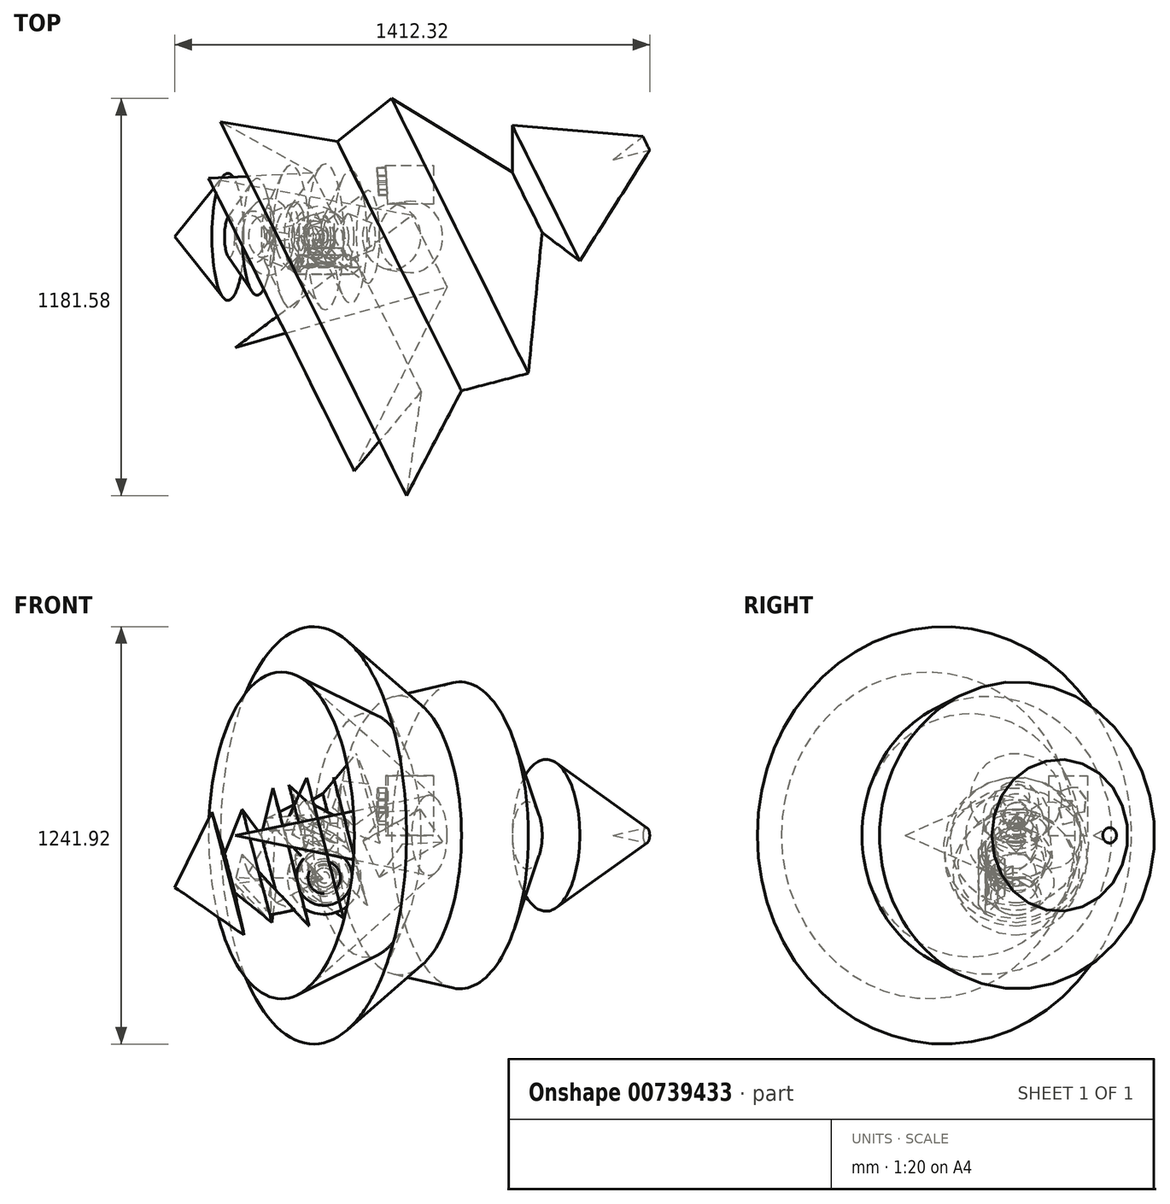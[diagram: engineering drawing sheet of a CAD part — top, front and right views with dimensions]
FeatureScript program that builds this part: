
annotation { "Feature Type Name" : "Feature", "Feature Type Description" : "" }
export const myFeature = defineFeature(function(context is Context, id is Id, definition is map)
    precondition{}
    {
        {
            var Q0;
            Q0=qCreatedBy(makeId("Front.planeOp"),FACE);
            var sketch = newSketch(context, id + "F0", { "sketchPlane" : qUnion([Q0])});
            skLineSegment(sketch, "E0", {"start": v(-2.63, 51.59) * mm, "end": v(-55.72, -50.08) * mm});
            skLineSegment(sketch, "E1", {"start": v(-55.72, -50.08) * mm, "end": v(-14.15, -31.55) * mm});
            skLineSegment(sketch, "E2", {"start": v(-14.15, -31.55) * mm, "end": v(-23.57, -10.42) * mm});
            skLineSegment(sketch, "E3", {"start": v(-23.57, -10.42) * mm, "end": v(10.4, -53.09) * mm});
            skLineSegment(sketch, "E4", {"start": v(10.4, -53.09) * mm, "end": v(32.93, -22.29) * mm});
            skLineSegment(sketch, "E5", {"start": v(32.93, -22.29) * mm, "end": v(13.65, -17.28) * mm});
            skLineSegment(sketch, "E6", {"start": v(13.65, -17.28) * mm, "end": v(30.68, 3.5) * mm});
            skLineSegment(sketch, "E7", {"start": v(30.68, 3.5) * mm, "end": v(61.07, -21.4) * mm});
            skLineSegment(sketch, "E8", {"start": v(61.07, -21.4) * mm, "end": v(73.25, 36.31) * mm});
            skLineSegment(sketch, "E9", {"start": v(73.25, 36.31) * mm, "end": v(11.4, 36.31) * mm});
            skLineSegment(sketch, "E10", {"start": v(11.4, 36.31) * mm, "end": v(0.63, -7.51) * mm});
            skLineSegment(sketch, "E11", {"start": v(0.63, -7.51) * mm, "end": v(-2.63, 51.59) * mm});
            skSolve(sketch);
        }
        {
            var Q0;
            Q0=makeQuery(id+"F0.imprint","IMPRINT",FACE,{"disambiguationData":[TD([[makeQuery(id+"F0.imprint","IMPRINT",EDGE,{"derivedFrom":sQuery(id+"F0.wireOp",EDGE,"E0")}),1.0]])]});
            var Q1;
            Q1=sQuery(id+"F0.wireOp",EDGE,"E0");
            revolve(context, id + "F1", {"surfaceOperationType" : NewSurfaceOperationType.NEW, "entities" : qUnion([Q0]), "axis" : qUnion([Q1]), "revolveType" : RevolveType.FULL});
        }
        {
            var Q0;
            Q0=qCreatedBy(makeId("Right.planeOp"),FACE);
            var sketch = newSketch(context, id + "F2", { "sketchPlane" : qUnion([Q0])});
            skLineSegment(sketch, "E12", {"start": v(-33.87, -70.47) * mm, "end": v(-87.06, -44.3) * mm});
            skLineSegment(sketch, "E13", {"start": v(-87.06, -44.3) * mm, "end": v(-53.53, -50.85) * mm});
            skLineSegment(sketch, "E14", {"start": v(-53.53, -50.85) * mm, "end": v(-90.7, -16.17) * mm});
            skLineSegment(sketch, "E15", {"start": v(-90.7, -16.17) * mm, "end": v(-110.94, -42.5) * mm});
            skLineSegment(sketch, "E16", {"start": v(-110.94, -42.5) * mm, "end": v(-80.24, -77.64) * mm});
            skLineSegment(sketch, "E17", {"start": v(-80.24, -77.64) * mm, "end": v(-88.69, -125.64) * mm});
            skLineSegment(sketch, "E18", {"start": v(-88.69, -125.64) * mm, "end": v(-55.2, -125.64) * mm});
            skLineSegment(sketch, "E19", {"start": v(-55.2, -125.64) * mm, "end": v(-75.07, -97.2) * mm});
            skLineSegment(sketch, "E20", {"start": v(-75.07, -97.2) * mm, "end": v(-62.68, -85.31) * mm});
            skLineSegment(sketch, "E21", {"start": v(-62.68, -85.31) * mm, "end": v(-31.96, -109.17) * mm});
            skLineSegment(sketch, "E22", {"start": v(-31.96, -109.17) * mm, "end": v(-9.41, -89.97) * mm});
            skLineSegment(sketch, "E23", {"start": v(-9.41, -89.97) * mm, "end": v(-33.87, -97.57) * mm});
            skLineSegment(sketch, "E24", {"start": v(-33.87, -97.57) * mm, "end": v(-33.87, -70.47) * mm});
            skSolve(sketch);
        }
        {
            var Q0;
            Q0=makeQuery(id+"F2.imprint","IMPRINT",FACE,{"disambiguationData":[TD([[makeQuery(id+"F2.imprint","IMPRINT",EDGE,{"derivedFrom":sQuery(id+"F2.wireOp",EDGE,"E12")}),1.0]])]});
            var Q1;
            Q1=sQuery(id+"F2.wireOp",EDGE,"E18");
            revolve(context, id + "F3", {"surfaceOperationType" : NewSurfaceOperationType.NEW, "entities" : qUnion([Q0]), "axis" : qUnion([Q1]), "revolveType" : RevolveType.FULL});
        }
        {
            var Q0;
            Q0=qCreatedBy(makeId("Front.planeOp"),FACE);
            var sketch = newSketch(context, id + "F4", { "sketchPlane" : qUnion([Q0])});
            skLineSegment(sketch, "E25", {"start": v(178.62, 69.18) * mm, "end": v(114.89, -17.47) * mm});
            skLineSegment(sketch, "E26", {"start": v(114.89, -17.47) * mm, "end": v(162.96, -124.25) * mm});
            skLineSegment(sketch, "E27", {"start": v(162.96, -124.25) * mm, "end": v(231.73, -26.42) * mm});
            skLineSegment(sketch, "E28", {"start": v(231.73, -26.42) * mm, "end": v(178.62, 69.18) * mm});
            skSolve(sketch);
        }
        {
            var Q0;
            Q0=makeQuery(id+"F4.imprint","IMPRINT",FACE,{"disambiguationData":[TD([[makeQuery(id+"F4.imprint","IMPRINT",EDGE,{"derivedFrom":sQuery(id+"F4.wireOp",EDGE,"E25")}),1.0]])]});
            var Q1;
            Q1=sQuery(id+"F4.wireOp",EDGE,"E28");
            revolve(context, id + "F5", {"surfaceOperationType" : NewSurfaceOperationType.NEW, "entities" : qUnion([Q0]), "axis" : qUnion([Q1]), "revolveType" : RevolveType.FULL});
        }
        {
            var Q0;
            Q0=qCreatedBy(makeId("Front.planeOp"),FACE);
            var sketch = newSketch(context, id + "F6", { "sketchPlane" : qUnion([Q0])});
            skLineSegment(sketch, "E29", {"start": v(-225.5, -112.51) * mm, "end": v(-146.12, 21.1) * mm});
            skLineSegment(sketch, "E30", {"start": v(-146.12, 21.1) * mm, "end": v(-151.15, -125.37) * mm});
            skLineSegment(sketch, "E31", {"start": v(-151.15, -125.37) * mm, "end": v(-228.86, -198.6) * mm});
            skLineSegment(sketch, "E32", {"start": v(-228.86, -198.6) * mm, "end": v(-264.64, -144.38) * mm});
            skLineSegment(sketch, "E33", {"start": v(-264.64, -144.38) * mm, "end": v(-176.87, -132.64) * mm});
            skLineSegment(sketch, "E34", {"start": v(-176.87, -132.64) * mm, "end": v(-262.4, -125.93) * mm});
            skLineSegment(sketch, "E35", {"start": v(-262.4, -125.93) * mm, "end": v(-243.96, -56.6) * mm});
            skLineSegment(sketch, "E36", {"start": v(-243.96, -56.6) * mm, "end": v(-225.5, -112.51) * mm});
            skSolve(sketch);
        }
        {
            var Q0;
            Q0 = qSketchRegion(id + "F6", true);
            var Q1;
            Q1=sQuery(id+"F6.wireOp",EDGE,"E31");
            revolve(context, id + "F7", {"operationType" : NewBodyOperationType.ADD, "surfaceOperationType" : NewSurfaceOperationType.NEW, "entities" : qUnion([Q0]), "axis" : qUnion([Q1]), "revolveType" : RevolveType.FULL});
        }
        {
            var Q0;
            Q0=qCreatedBy(makeId("Front.planeOp"),FACE);
            var sketch = newSketch(context, id + "F8", { "sketchPlane" : qUnion([Q0])});
            skLineSegment(sketch, "E37", {"start": v(19.88, 31.76) * mm, "end": v(165.14, -22.85) * mm});
            skLineSegment(sketch, "E38", {"start": v(165.14, -22.85) * mm, "end": v(152.75, 74) * mm});
            skLineSegment(sketch, "E39", {"start": v(152.75, 74) * mm, "end": v(88.57, 28.39) * mm});
            skLineSegment(sketch, "E40", {"start": v(88.57, 28.39) * mm, "end": v(25.5, 82.44) * mm});
            skLineSegment(sketch, "E41", {"start": v(25.5, 82.44) * mm, "end": v(-60.08, 59.92) * mm});
            skLineSegment(sketch, "E42", {"start": v(-60.08, 59.92) * mm, "end": v(-161.99, 13.18) * mm});
            skLineSegment(sketch, "E43", {"start": v(-161.99, 13.18) * mm, "end": v(-58.95, 19.38) * mm});
            skLineSegment(sketch, "E44", {"start": v(-58.95, 19.38) * mm, "end": v(-55.33, -40.89) * mm});
            skLineSegment(sketch, "E45", {"start": v(-55.33, -40.89) * mm, "end": v(-31.36, 32.33) * mm});
            skLineSegment(sketch, "E46", {"start": v(-31.36, 32.33) * mm, "end": v(19.88, 31.76) * mm});
            skSolve(sketch);
        }
        {
            var Q0;
            Q0=makeQuery(id+"F8.imprint","IMPRINT",FACE,{"disambiguationData":[TD([[makeQuery(id+"F8.imprint","IMPRINT",EDGE,{"derivedFrom":sQuery(id+"F8.wireOp",EDGE,"E37")}),1.0]])]});
            var Q1;
            Q1=sQuery(id+"F8.wireOp",EDGE,"E41");
            revolve(context, id + "F9", {"surfaceOperationType" : NewSurfaceOperationType.NEW, "entities" : qUnion([Q0]), "axis" : qUnion([Q1]), "revolveType" : RevolveType.FULL});
        }
        {
            var Q0;
            Q0=qCreatedBy(makeId("Front.planeOp"),FACE);
            var sketch = newSketch(context, id + "F10", { "sketchPlane" : qUnion([Q0])});
            skLineSegment(sketch, "E47", {"start": v(67.32, -21.03) * mm, "end": v(-444.16, -155.22) * mm});
            skLineSegment(sketch, "E48", {"start": v(-444.16, -155.22) * mm, "end": v(-334.45, 68.95) * mm});
            skLineSegment(sketch, "E49", {"start": v(-334.45, 68.95) * mm, "end": v(-296.56, -54.19) * mm});
            skLineSegment(sketch, "E50", {"start": v(-296.56, -54.19) * mm, "end": v(-243.68, 76.84) * mm});
            skLineSegment(sketch, "E51", {"start": v(-243.68, 76.84) * mm, "end": v(-187.63, 0) * mm});
            skLineSegment(sketch, "E52", {"start": v(-187.63, 0) * mm, "end": v(-152.9, 140.78) * mm});
            skLineSegment(sketch, "E53", {"start": v(-152.9, 140.78) * mm, "end": v(-118.96, 23.17) * mm});
            skLineSegment(sketch, "E54", {"start": v(-118.96, 23.17) * mm, "end": v(-51.87, 171.56) * mm});
            skLineSegment(sketch, "E55", {"start": v(-51.87, 171.56) * mm, "end": v(-11.62, 22.38) * mm});
            skLineSegment(sketch, "E56", {"start": v(-11.62, 22.38) * mm, "end": v(27.85, 172.35) * mm});
            skLineSegment(sketch, "E57", {"start": v(27.85, 172.35) * mm, "end": v(67.32, -21.03) * mm});
            skSolve(sketch);
        }
        {
            var Q0;
            Q0 = qSketchRegion(id + "F10", true);
            var Q1;
            Q1=sQuery(id+"F10.wireOp",EDGE,"E47");
            revolve(context, id + "F11", {"surfaceOperationType" : NewSurfaceOperationType.NEW, "entities" : qUnion([Q0]), "axis" : qUnion([Q1]), "revolveType" : RevolveType.FULL});
        }
        {
            var Q0;
            Q0=qCreatedBy(makeId("Top.planeOp"),FACE);
            var sketch = newSketch(context, id + "F12", { "sketchPlane" : qUnion([Q0])});
            skLineSegment(sketch, "E58", {"start": v(182.68, 212.5) * mm, "end": v(325.44, 212.5) * mm});
            skLineSegment(sketch, "E59", {"start": v(325.44, 212.5) * mm, "end": v(325.44, 96.64) * mm});
            skLineSegment(sketch, "E60", {"start": v(325.44, 96.64) * mm, "end": v(189.03, 96.64) * mm});
            skLineSegment(sketch, "E61", {"start": v(189.03, 96.64) * mm, "end": v(182.68, 212.5) * mm});
            skSolve(sketch);
        }
        {
            var Q0;
            Q0 = qSketchRegion(id + "F12", true);
            extrude(context, id + "F13", {"entities" : qUnion([Q0]), "operationType" : NewBodyOperationType.ADD, "depth" : 177.8 * mm, "offsetDistance" : 25.4 * mm});
        }
        {
            var Q0;
            Q0=makeQuery(id+"F13.opExtrude","SWEPT_FACE",FACE,{"disambiguationData":[OSD([sQuery(id+"F12.wireOp",EDGE,"E61")])]});
            var sketch = newSketch(context, id + "F14", { "sketchPlane" : qUnion([Q0])});
            skLineSegment(sketch, "E62", {"start": v(-198.04, 108.68) * mm, "end": v(-174.34, 142.32) * mm});
            skLineSegment(sketch, "E63", {"start": v(-174.34, 142.32) * mm, "end": v(-152.34, 142.32) * mm});
            skLineSegment(sketch, "E64", {"start": v(-152.34, 142.32) * mm, "end": v(-113.37, 127.19) * mm});
            skLineSegment(sketch, "E65", {"start": v(-113.37, 127.19) * mm, "end": v(-132.83, 104.26) * mm});
            skLineSegment(sketch, "E66", {"start": v(-132.83, 104.26) * mm, "end": v(-158.3, 104.26) * mm});
            skLineSegment(sketch, "E67", {"start": v(-158.3, 104.26) * mm, "end": v(-146, 86.21) * mm});
            skLineSegment(sketch, "E68", {"start": v(-146, 86.21) * mm, "end": v(-117.3, 81) * mm});
            skLineSegment(sketch, "E69", {"start": v(-117.3, 81) * mm, "end": v(-130.28, 32.3) * mm});
            skLineSegment(sketch, "E70", {"start": v(-130.28, 32.3) * mm, "end": v(-170.41, 42.98) * mm});
            skLineSegment(sketch, "E71", {"start": v(-170.41, 42.98) * mm, "end": v(-170.41, 66.92) * mm});
            skLineSegment(sketch, "E72", {"start": v(-170.41, 66.92) * mm, "end": v(-194.6, 70.63) * mm});
            skLineSegment(sketch, "E73", {"start": v(-194.6, 70.63) * mm, "end": v(-198.04, 108.68) * mm});
            skSolve(sketch);
        }
        {
            var Q0;
            Q0 = qSketchRegion(id + "F14", true);
            extrude(context, id + "F15", {"entities" : qUnion([Q0]), "operationType" : NewBodyOperationType.ADD, "depth" : 25.4 * mm, "offsetDistance" : 25.4 * mm});
        }
        {
            var Q0;
            Q0=qCreatedBy(makeId("Top.planeOp"),FACE);
            var sketch = newSketch(context, id + "F16", { "sketchPlane" : qUnion([Q0])});
            skLineSegment(sketch, "E74", {"start": v(947.82, 298.92) * mm, "end": v(859.88, 229.68) * mm});
            skLineSegment(sketch, "E75", {"start": v(-264.26, -329.44) * mm, "end": v(859.88, 229.68) * mm});
            skLineSegment(sketch, "E76", {"start": v(947.82, 298.92) * mm, "end": v(559.18, 332.28) * mm});
            skLineSegment(sketch, "E77", {"start": v(559.18, 332.28) * mm, "end": v(559.18, 191.79) * mm});
            skLineSegment(sketch, "E78", {"start": v(559.18, 191.79) * mm, "end": v(200.64, 411.76) * mm});
            skLineSegment(sketch, "E79", {"start": v(200.64, 411.76) * mm, "end": v(38.78, 284.34) * mm});
            skLineSegment(sketch, "E80", {"start": v(38.78, 284.34) * mm, "end": v(-308.36, 342.15) * mm});
            skLineSegment(sketch, "E81", {"start": v(-308.36, 342.15) * mm, "end": v(-34.5, 190.03) * mm});
            skLineSegment(sketch, "E82", {"start": v(-34.5, 190.03) * mm, "end": v(-344.02, 174.3) * mm});
            skLineSegment(sketch, "E83", {"start": v(-344.02, 174.3) * mm, "end": v(259.96, 63.83) * mm});
            skLineSegment(sketch, "E84", {"start": v(259.96, 63.83) * mm, "end": v(-264.26, -329.44) * mm});
            skSolve(sketch);
        }
        {
            var Q0;
            Q0 = qSketchRegion(id + "F16", true);
            var Q1;
            Q1=sQuery(id+"F16.wireOp",EDGE,"E75");
            revolve(context, id + "F17", {"surfaceOperationType" : NewSurfaceOperationType.NEW, "entities" : qUnion([Q0]), "axis" : qUnion([Q1]), "revolveType" : RevolveType.FULL});
        }
    });
